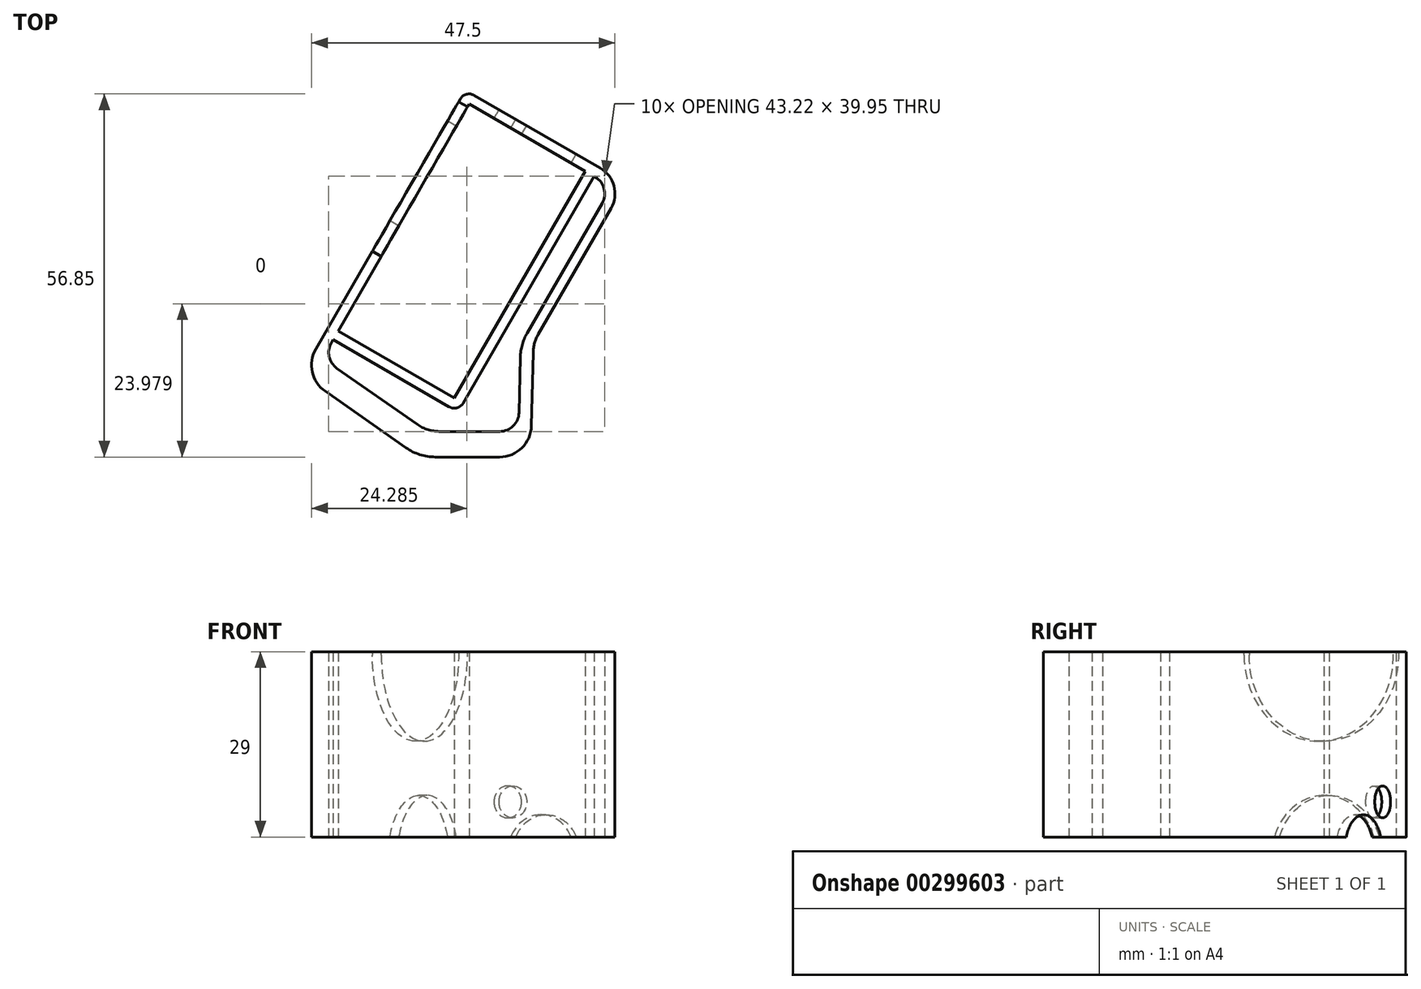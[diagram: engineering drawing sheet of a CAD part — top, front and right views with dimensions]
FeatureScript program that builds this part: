
annotation { "Feature Type Name" : "Feature", "Feature Type Description" : "" }
export const myFeature = defineFeature(function(context is Context, id is Id, definition is map)
    precondition{}
    {
        {
            var Q0;
            Q0=qCreatedBy(makeId("Top.planeOp"),FACE);
            var sketch = newSketch(context, id + "F0", { "sketchPlane" : qUnion([Q0])});
            skLineSegment(sketch, "E0.bottom", {"start": v(-19.08, 53.17) * mm, "end": v(-37.26, 63.67) * mm});
            skLineSegment(sketch, "E0.top", {"start": v(-39.58, 17.67) * mm, "end": v(-57.76, 28.17) * mm});
            skLineSegment(sketch, "E0.left", {"start": v(-19.08, 53.17) * mm, "end": v(-39.58, 17.67) * mm});
            skLineSegment(sketch, "E0.right", {"start": v(-37.26, 63.67) * mm, "end": v(-57.76, 28.17) * mm});
            skLineSegment(sketch, "E1", {"start": v(0, 0) * mm, "end": v(0, 58.57) * mm, "construction": true});
            skLineSegment(sketch, "E2", {"start": v(0, 0) * mm, "end": v(-67.03, 0) * mm, "construction": true});
            skLineSegment(sketch, "E3.0", {"start": v(-40.38, 16.28) * mm, "end": v(-58.56, 26.78) * mm});
            skLineSegment(sketch, "E3.1", {"start": v(-17.7, 52.37) * mm, "end": v(-38.2, 16.87) * mm});
            skLineSegment(sketch, "E3.2", {"start": v(-16.72, 53.66) * mm, "end": v(-36.46, 65.06) * mm});
            skLineSegment(sketch, "E3.3", {"start": v(-38.65, 64.47) * mm, "end": v(-59.95, 27.58) * mm});
            skLineSegment(sketch, "E4", {"start": v(-59.95, 27.58) * mm, "end": v(-61.25, 25.32) * mm});
            skLineSegment(sketch, "E5", {"start": v(-59.8, 18.73) * mm, "end": v(-47.15, 9.87) * mm});
            skLineSegment(sketch, "E6", {"start": v(-42.56, 8.42) * mm, "end": v(-32.5, 8.42) * mm});
            skLineSegment(sketch, "E7", {"start": v(-27.5, 13.3) * mm, "end": v(-27.22, 24.8) * mm});
            skLineSegment(sketch, "E8", {"start": v(-26.42, 27.66) * mm, "end": v(-15.03, 47.37) * mm});
            skLineSegment(sketch, "E9", {"start": v(-16.72, 53.66) * mm, "end": v(-16.72, 53.66) * mm});
            skLineSegment(sketch, "E10", {"start": v(-58.56, 26.78) * mm, "end": v(-58.85, 26.3) * mm});
            skLineSegment(sketch, "E11", {"start": v(-57.97, 22.33) * mm, "end": v(-45.37, 13.5) * mm});
            skLineSegment(sketch, "E12", {"start": v(-41.93, 12.42) * mm, "end": v(-32.44, 12.42) * mm});
            skLineSegment(sketch, "E13", {"start": v(-29.24, 24.02) * mm, "end": v(-29.44, 15.35) * mm});
            skLineSegment(sketch, "E14", {"start": v(-17.7, 52.37) * mm, "end": v(-17.52, 52.27) * mm});
            skLineSegment(sketch, "E15", {"start": v(-28.17, 27.83) * mm, "end": v(-16.42, 48.17) * mm});
            skPoint(sketch, "E16.visualSharp", {"position": v(-12.73, 51.36) * mm});
            skArc(sketch, "E16.filletArc", {"start": v(-15.03, 47.37) * mm, "mid": v(-14.57, 50.87) * mm, "end": v(-16.72, 53.66) * mm});
            skPoint(sketch, "E17.visualSharp", {"position": v(-14.92, 50.77) * mm});
            skArc(sketch, "E17.filletArc", {"start": v(-16.42, 48.17) * mm, "mid": v(-16.12, 50.45) * mm, "end": v(-17.52, 52.27) * mm});
            skPoint(sketch, "E18.visualSharp", {"position": v(-27.18, 26.34) * mm});
            skArc(sketch, "E18.filletArc", {"start": v(-26.42, 27.66) * mm, "mid": v(-27, 26.28) * mm, "end": v(-27.22, 24.8) * mm});
            skPoint(sketch, "E19.visualSharp", {"position": v(-29.19, 26.06) * mm});
            skArc(sketch, "E19.filletArc", {"start": v(-28.17, 27.83) * mm, "mid": v(-28.94, 26) * mm, "end": v(-29.24, 24.02) * mm});
            skPoint(sketch, "E20.visualSharp", {"position": v(-29.51, 12.42) * mm});
            skArc(sketch, "E20.filletArc", {"start": v(-32.44, 12.42) * mm, "mid": v(-30.35, 13.28) * mm, "end": v(-29.44, 15.35) * mm});
            skPoint(sketch, "E21.visualSharp", {"position": v(-27.6, 8.42) * mm});
            skArc(sketch, "E21.filletArc", {"start": v(-32.5, 8.42) * mm, "mid": v(-29, 9.85) * mm, "end": v(-27.5, 13.3) * mm});
            skPoint(sketch, "E22.visualSharp", {"position": v(-43.82, 12.42) * mm});
            skArc(sketch, "E22.filletArc", {"start": v(-45.37, 13.5) * mm, "mid": v(-43.73, 12.7) * mm, "end": v(-41.93, 12.42) * mm});
            skPoint(sketch, "E23.visualSharp", {"position": v(-45.08, 8.42) * mm});
            skArc(sketch, "E23.filletArc", {"start": v(-47.15, 9.87) * mm, "mid": v(-44.96, 8.8) * mm, "end": v(-42.56, 8.42) * mm});
            skPoint(sketch, "E24.visualSharp", {"position": v(-60.22, 23.9) * mm});
            skArc(sketch, "E24.filletArc", {"start": v(-58.85, 26.3) * mm, "mid": v(-59.18, 24.14) * mm, "end": v(-57.97, 22.33) * mm});
            skPoint(sketch, "E25.visualSharp", {"position": v(-63.54, 21.35) * mm});
            skArc(sketch, "E25.filletArc", {"start": v(-61.25, 25.32) * mm, "mid": v(-61.8, 21.74) * mm, "end": v(-59.8, 18.73) * mm});
            skPoint(sketch, "E26.visualSharp", {"position": v(-37.85, 65.86) * mm});
            skArc(sketch, "E26.filletArc", {"start": v(-36.46, 65.06) * mm, "mid": v(-37.68, 65.22) * mm, "end": v(-38.65, 64.47) * mm});
            skPoint(sketch, "E27.visualSharp", {"position": v(-39, 15.48) * mm});
            skArc(sketch, "E27.filletArc", {"start": v(-40.38, 16.28) * mm, "mid": v(-39.16, 16.12) * mm, "end": v(-38.2, 16.87) * mm});
            skLineSegment(sketch, "E28", {"start": v(-42.56, 8.42) * mm, "end": v(-45.08, 8.42) * mm, "construction": true});
            skLineSegment(sketch, "E29", {"start": v(-47.15, 9.87) * mm, "end": v(-45.08, 8.42) * mm, "construction": true});
            skLineSegment(sketch, "E30", {"start": v(-53.47, 14.3) * mm, "end": v(-67.71, -6.04) * mm, "construction": true});
            skSolve(sketch);
        }
        {
            var Q0;
            Q0=makeQuery(id+"F0.imprint","IMPRINT",FACE,{"disambiguationData":[TD([[makeQuery(id+"F0.imprint","IMPRINT",EDGE,{"derivedFrom":sQuery(id+"F0.wireOp",EDGE,"E0.bottom")}),-1.0]])]});
            extrude(context, id + "F1", {"entities" : qUnion([Q0]), "depth" : 29 * mm});
        }
        {
            var Q0;
            Q0=makeQuery(id+"F1.opExtrude","SWEPT_FACE",FACE,{"disambiguationData":[OSD([sQuery(id+"F0.wireOp",EDGE,"E3.3"),sQuery(id+"F0.wireOp",EDGE,"E4")])]});
            var sketch = newSketch(context, id + "F2", { "sketchPlane" : qUnion([Q0])});
            skLineSegment(sketch, "E31", {"start": v(-36.51, 14.5) * mm, "end": v(8.7, 14.5) * mm, "construction": true});
            skCircle(sketch, "E32", {"center": v(-22.51, 28.5) * mm, "radius": 13.5 * mm});
            skCircle(sketch, "E33", {"center": v(-23.51, -3) * mm, "radius": 9.5 * mm});
            skLineSegment(sketch, "E34", {"start": v(-9.01, 29) * mm, "end": v(-9.01, 28.5) * mm});
            skLineSegment(sketch, "E35", {"start": v(-36.01, 29) * mm, "end": v(-36.01, 28.5) * mm});
            skLineSegment(sketch, "E36", {"start": v(-14.01, -3) * mm, "end": v(-14.01, 0) * mm});
            skLineSegment(sketch, "E37", {"start": v(-33.01, -3) * mm, "end": v(-33.01, 0) * mm});
            skPoint(sketch, "E38.middle", {"position": v(8.7, 14.5) * mm});
            skSolve(sketch);
        }
        {
            var Q0;
            Q0=makeQuery(id+"F1.opExtrude","SWEPT_FACE",FACE,{"disambiguationData":[OSD([sQuery(id+"F0.wireOp",EDGE,"E3.2")])]});
            var sketch = newSketch(context, id + "F3", { "sketchPlane" : qUnion([Q0])});
            skLineSegment(sketch, "E39", {"start": v(41.3, 14.5) * mm, "end": v(64.1, 14.5) * mm, "construction": true});
            skCircle(sketch, "E40", {"center": v(57.1, 5.5) * mm, "radius": 2.5 * mm});
            skCircle(sketch, "E41", {"center": v(51.1, -2.5) * mm, "radius": 6 * mm});
            skSolve(sketch);
        }
        {
            var Q0;
            {var subQ0=sQuery(id+"F2.wireOp",EDGE,"E32");var subQ1=makeQuery(id+"F2.imprint","INTERSECT",VERTEX,{"derivedFrom":[subQ0,sQuery(id+"F2.wireOp",EDGE,"E34")]});Q0=makeQuery(id+"F2.imprint","IMPRINT",FACE,{"disambiguationData":[TD([[makeQuery(id+"F2.imprint","IMPRINT",EDGE,{"disambiguationData":[TD([[subQ1,1.0]])],"derivedFrom":subQ0}),1.0]])]});}
            var Q1;
            {var subQ0=sQuery(id+"F2.wireOp",EDGE,"E34");Q1=makeQuery(id+"F2.imprint","IMPRINT",FACE,{"disambiguationData":[TD([[makeQuery(id+"F2.imprint","IMPRINT",EDGE,{"derivedFrom":subQ0}),-1.0]])]});}
            var Q2;
            {var subQ0=sQuery(id+"F2.wireOp",EDGE,"E33");var subQ1=makeQuery(id+"F1.opExtrude","CAP_EDGE",EDGE,{"disambiguationData":[OSD([sQuery(id+"F0.wireOp",EDGE,"E3.3"),sQuery(id+"F0.wireOp",EDGE,"E4")])],"isStart":true});var subQ2=makeQuery(id+"F2.imprint","INTERSECT",VERTEX,{"disambiguationData":[OD(0.0)],"derivedFrom":[subQ1,subQ0]});Q2=makeQuery(id+"F2.imprint","IMPRINT",FACE,{"disambiguationData":[TD([[makeQuery(id+"F2.imprint","IMPRINT",EDGE,{"disambiguationData":[TD([[subQ2,-1.0]])],"derivedFrom":subQ0}),1.0]])]});}
            extrude(context, id + "F4", {"entities" : qUnion([Q0, Q1, Q2]), "operationType" : NewBodyOperationType.REMOVE, "oppositeDirection" : true, "depth" : 2 * mm});
        }
        {
            var Q0;
            {var subQ0=sQuery(id+"F3.wireOp",EDGE,"E41");var subQ1=makeQuery(id+"F1.opExtrude","CAP_EDGE",EDGE,{"disambiguationData":[OSD([sQuery(id+"F0.wireOp",EDGE,"E3.2")])],"isStart":true});var subQ2=makeQuery(id+"F3.imprint","INTERSECT",VERTEX,{"disambiguationData":[OD(0.0)],"derivedFrom":[subQ1,subQ0]});Q0=makeQuery(id+"F3.imprint","IMPRINT",FACE,{"disambiguationData":[TD([[makeQuery(id+"F3.imprint","IMPRINT",EDGE,{"disambiguationData":[TD([[subQ2,1.0]])],"derivedFrom":subQ0}),1.0]])]});}
            var Q1;
            Q1=makeQuery(id+"F3.imprint","IMPRINT",FACE,{"disambiguationData":[TD([[makeQuery(id+"F3.imprint","IMPRINT",EDGE,{"derivedFrom":sQuery(id+"F3.wireOp",EDGE,"E40")}),1.0]])]});
            extrude(context, id + "F5", {"entities" : qUnion([Q0, Q1]), "operationType" : NewBodyOperationType.REMOVE, "oppositeDirection" : true, "depth" : 2 * mm});
        }
    });
